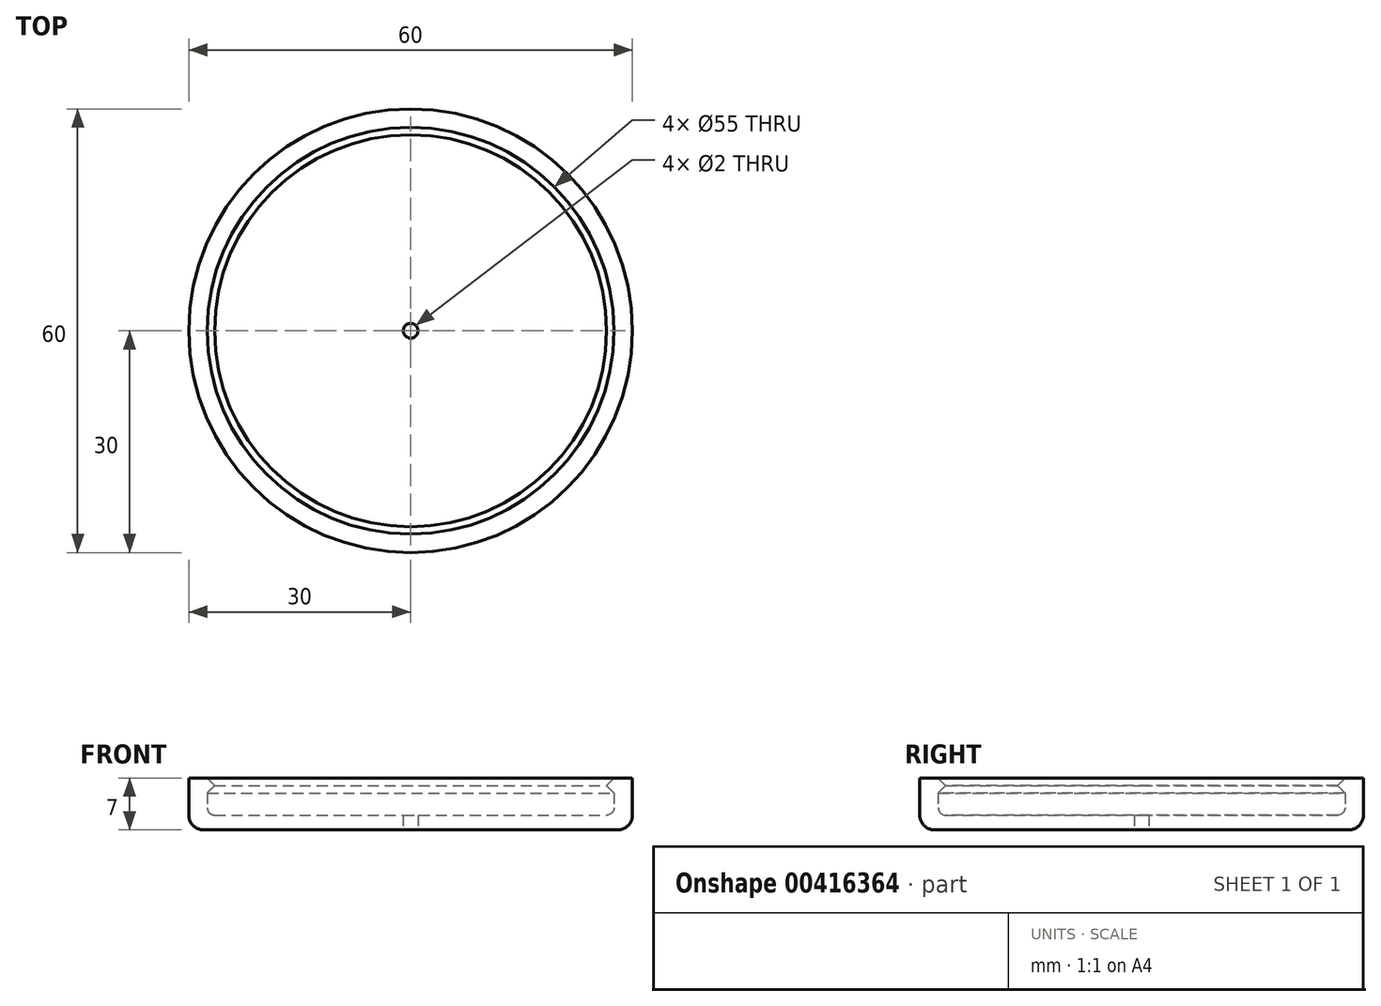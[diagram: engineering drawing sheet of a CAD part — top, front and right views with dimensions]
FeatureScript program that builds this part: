
annotation { "Feature Type Name" : "Feature", "Feature Type Description" : "" }
export const myFeature = defineFeature(function(context is Context, id is Id, definition is map)
    precondition{}
    {
        {
            var Q0;
            Q0=qCreatedBy(makeId("Front.planeOp"),FACE);
            var sketch = newSketch(context, id + "F0", { "sketchPlane" : qUnion([Q0])});
            skLineSegment(sketch, "E0", {"start": v(0, 0) * mm, "end": v(0, 2) * mm});
            skLineSegment(sketch, "E1", {"start": v(0, 2) * mm, "end": v(-26.5, 2) * mm});
            skLineSegment(sketch, "E2", {"start": v(-27.5, 3) * mm, "end": v(-27.5, 5) * mm});
            skLineSegment(sketch, "E3", {"start": v(-27.5, 5) * mm, "end": v(-26.5, 6) * mm});
            skLineSegment(sketch, "E4", {"start": v(-26.5, 6) * mm, "end": v(-27.5, 7) * mm});
            skLineSegment(sketch, "E5", {"start": v(-27.5, 7) * mm, "end": v(-30, 7) * mm});
            skLineSegment(sketch, "E6", {"start": v(-30, 7) * mm, "end": v(-30, 2) * mm});
            skLineSegment(sketch, "E7", {"start": v(-28, 0) * mm, "end": v(0, 0) * mm});
            skPoint(sketch, "E8.visualSharp", {"position": v(-30, 0) * mm});
            skArc(sketch, "E8.filletArc", {"start": v(-30, 2) * mm, "mid": v(-29.41, 0.59) * mm, "end": v(-28, 0) * mm});
            skPoint(sketch, "E9.visualSharp", {"position": v(-27.5, 2) * mm});
            skArc(sketch, "E9.filletArc", {"start": v(-27.5, 3) * mm, "mid": v(-27.2, 2.3) * mm, "end": v(-26.5, 2) * mm});
            skSolve(sketch);
        }
        {
            var Q0;
            Q0=makeQuery(id+"F0.imprint","IMPRINT",FACE,{"disambiguationData":[TD([[makeQuery(id+"F0.imprint","IMPRINT",EDGE,{"derivedFrom":sQuery(id+"F0.wireOp",EDGE,"E0")}),1.0]])]});
            var Q1;
            Q1=sQuery(id+"F0.wireOp",EDGE,"E0");
            revolve(context, id + "F1", {"entities" : qUnion([Q0]), "axis" : qUnion([Q1]), "revolveType" : RevolveType.FULL});
        }
        {
            var Q0;
            Q0=makeQuery(id+"F1.opRevolve","SWEPT_FACE",FACE,{"disambiguationData":[OSD([sQuery(id+"F0.wireOp",EDGE,"E7")])]});
            var sketch = newSketch(context, id + "F2", { "sketchPlane" : qUnion([Q0])});
            skCircle(sketch, "E10", {"center": v(0, 0) * mm, "radius": 1 * mm});
            skSolve(sketch);
        }
        {
            var Q0;
            Q0=makeQuery(id+"F2.imprint","IMPRINT",FACE,{"disambiguationData":[TD([[makeQuery(id+"F2.imprint","IMPRINT",EDGE,{"derivedFrom":sQuery(id+"F2.wireOp",EDGE,"E10")}),1.0]])]});
            extrude(context, id + "F3", {"entities" : qUnion([Q0]), "operationType" : NewBodyOperationType.REMOVE, "oppositeDirection" : true, "depth" : 25 * mm});
        }
    });
